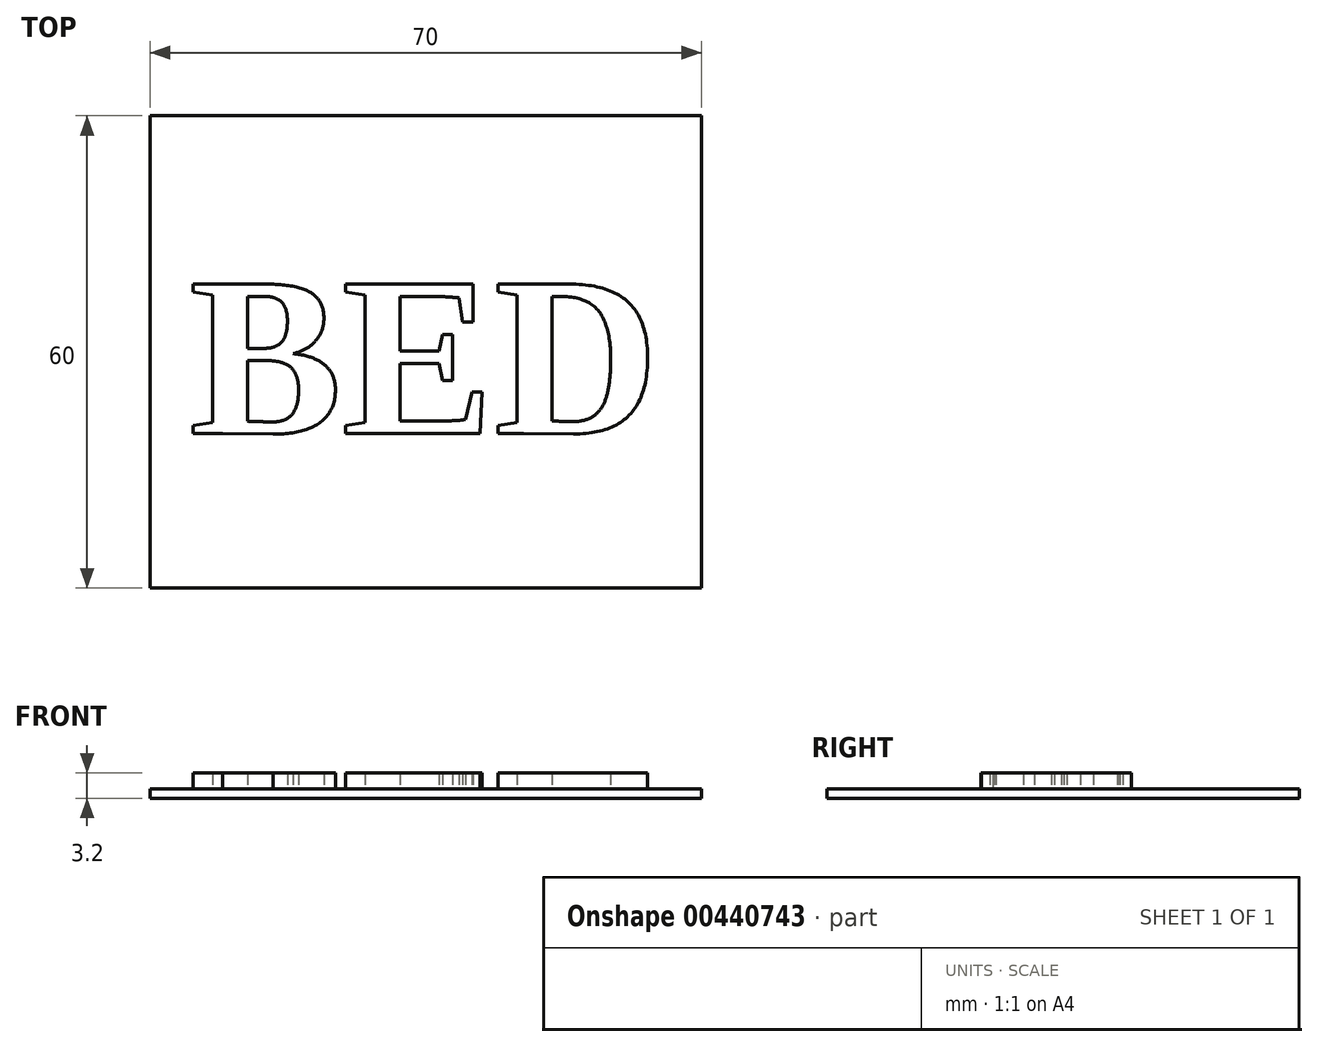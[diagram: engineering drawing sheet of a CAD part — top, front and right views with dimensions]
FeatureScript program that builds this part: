
annotation { "Feature Type Name" : "Feature", "Feature Type Description" : "" }
export const myFeature = defineFeature(function(context is Context, id is Id, definition is map)
    precondition{}
    {
        {
            var Q0;
            Q0=qCreatedBy(makeId("Top.planeOp"),FACE);
            var sketch = newSketch(context, id + "F0", { "sketchPlane" : qUnion([Q0])});
            skLineSegment(sketch, "E0.bottom", {"start": v(35, 30) * mm, "end": v(-35, 30) * mm});
            skLineSegment(sketch, "E0.top", {"start": v(35, -30) * mm, "end": v(-35, -30) * mm});
            skLineSegment(sketch, "E0.left", {"start": v(35, 30) * mm, "end": v(35, -30) * mm});
            skLineSegment(sketch, "E0.right", {"start": v(-35, 30) * mm, "end": v(-35, -30) * mm});
            skPoint(sketch, "E0.middle", {"position": v(0, 0) * mm});
            skSolve(sketch);
        }
        {
            var Q0;
            Q0 = qSketchRegion(id + "F0", true);
            extrude(context, id + "F1", {"entities" : qUnion([Q0]), "depth" : 1.2 * mm});
        }
        {
            var Q0;
            Q0=makeQuery(id+"F1.opExtrude","CAP_FACE",FACE,{"disambiguationData":[OSD([sQuery(id+"F0.wireOp",EDGE,"E0.bottom"),sQuery(id+"F0.wireOp",EDGE,"E0.top"),sQuery(id+"F0.wireOp",EDGE,"E0.left"),sQuery(id+"F0.wireOp",EDGE,"E0.right")])],"isStart":false});
            var sketch = newSketch(context, id + "F2", { "sketchPlane" : qUnion([Q0])});
            skText(sketch, "E1", { "text": "BED", "fontName": "Tinos-Bold.ttf"});
            const initialGuessF2  = {"E1": [-0.03, -0.01037, 1, 0, 0.02087]};
            skSetInitialGuess(sketch, initialGuessF2);
            skSolve(sketch);
        }
        {
            var Q0;
            Q0 = qSketchRegion(id + "F2", true);
            extrude(context, id + "F3", {"entities" : qUnion([Q0]), "operationType" : NewBodyOperationType.ADD, "depth" : 2 * mm});
        }
    });
